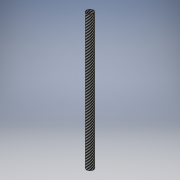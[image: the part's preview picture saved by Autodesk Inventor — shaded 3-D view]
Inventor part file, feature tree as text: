
AUTODESK INVENTOR PART (.ipt)
format: ipt  version: 2018 (Build 220112000, 112)  size: 109,568 bytes
history: native  units: in
note: dims shown in document units (in); Inventor stores cm internally (conversion verified against a paired STEP export)
features: extrude x1, sketch x1
ambient origin geometry x8: Origin, YZ Plane, XZ Plane, XY Plane, X Axis, Y Axis, Z Axis, Center Point
bodies: Solid1 (feature_tree)
feature tree (2):
  extrude  "Extrusion1"  Depth=7.9232in
  sketch  "Sketch1"  dims[d0=0.42in d1=0.39in d2=7.9232in d3=0.0in]
